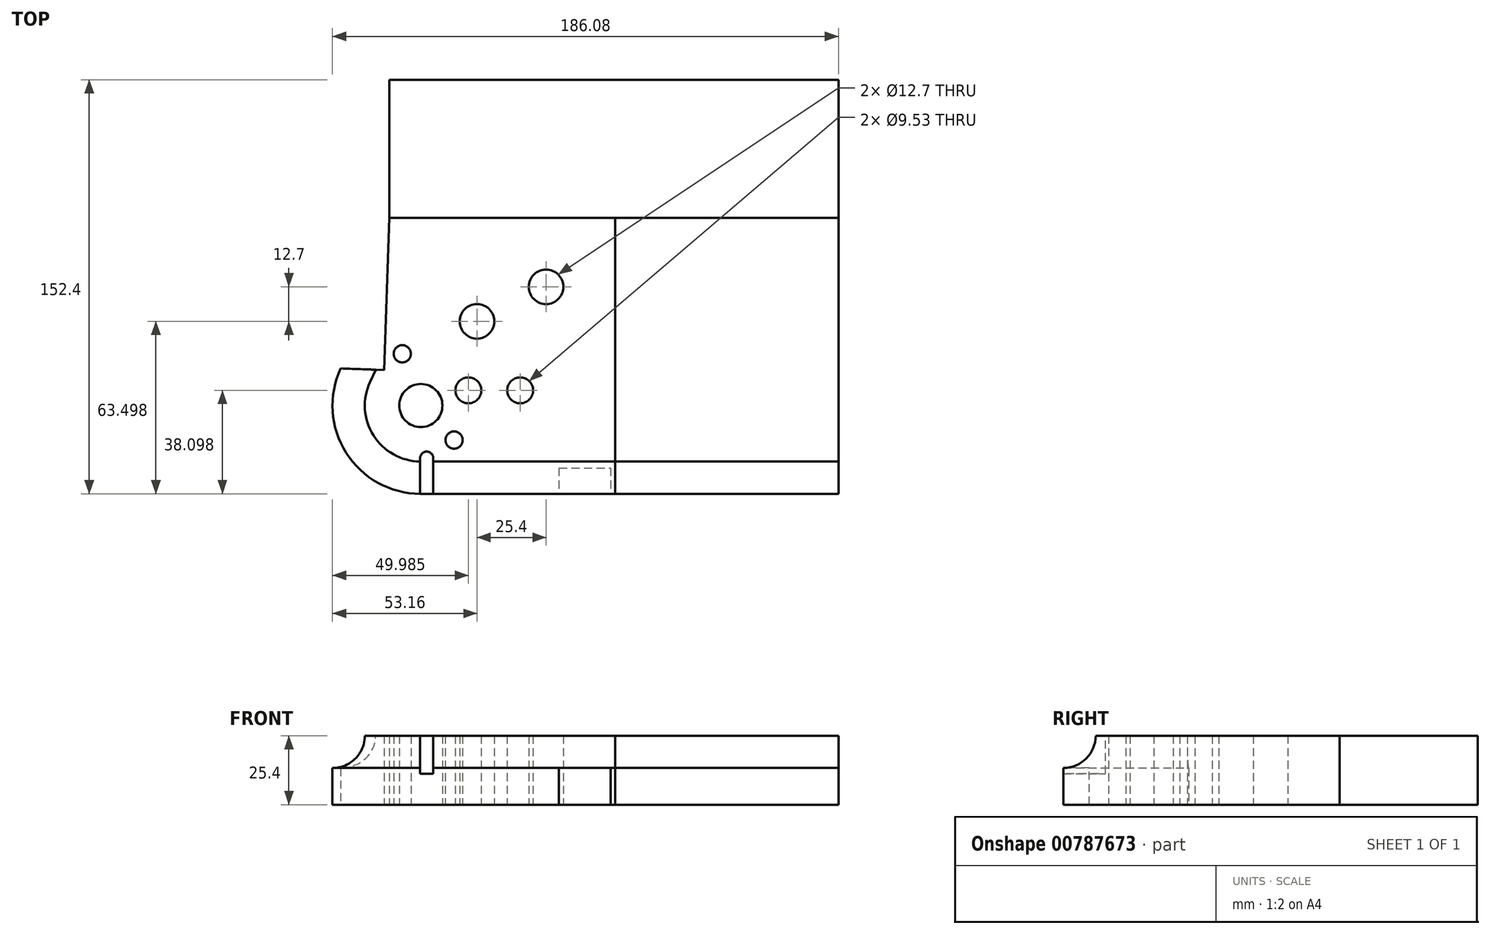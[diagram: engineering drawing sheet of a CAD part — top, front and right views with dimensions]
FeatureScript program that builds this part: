
annotation { "Feature Type Name" : "Feature", "Feature Type Description" : "" }
export const myFeature = defineFeature(function(context is Context, id is Id, definition is map)
    precondition{}
    {
        {
            var Q0;
            Q0=qCreatedBy(makeId("Top.planeOp"),FACE);
            var sketch = newSketch(context, id + "F0", { "sketchPlane" : qUnion([Q0])});
            skArc(sketch, "E0", {"start": v(-29.51, 13.64) * mm, "mid": v(-27.4, -17.51) * mm, "end": v(0, -32.51) * mm});
            skLineSegment(sketch, "E1", {"start": v(0, -32.51) * mm, "end": v(71.45, -32.51) * mm});
            skLineSegment(sketch, "E2", {"start": v(71.45, -32.51) * mm, "end": v(71.45, 69.09) * mm});
            skLineSegment(sketch, "E3", {"start": v(71.45, 69.09) * mm, "end": v(-11.53, 69.09) * mm});
            skLineSegment(sketch, "E4", {"start": v(-13.49, 13.08) * mm, "end": v(-29.51, 13.64) * mm});
            skLineSegment(sketch, "E5", {"start": v(-11.53, 69.09) * mm, "end": v(-13.49, 13.08) * mm});
            skCircle(sketch, "E6", {"center": v(0, 0) * mm, "radius": 7.94 * mm});
            skCircle(sketch, "E7", {"center": v(46.05, 43.69) * mm, "radius": 6.35 * mm});
            skCircle(sketch, "E8", {"center": v(20.65, 30.99) * mm, "radius": 6.35 * mm});
            skCircle(sketch, "E9", {"center": v(-6.83, 19.05) * mm, "radius": 3.18 * mm});
            skCircle(sketch, "E10", {"center": v(17.48, 5.59) * mm, "radius": 4.76 * mm});
            skCircle(sketch, "E11", {"center": v(36.53, 5.59) * mm, "radius": 4.76 * mm});
            skCircle(sketch, "E12", {"center": v(12.22, -12.7) * mm, "radius": 3.18 * mm});
            skSolve(sketch);
        }
        {
            var Q0;
            Q0=makeQuery(id+"F0.imprint","IMPRINT",FACE,{"disambiguationData":[TD([[makeQuery(id+"F0.imprint","IMPRINT",EDGE,{"derivedFrom":sQuery(id+"F0.wireOp",EDGE,"E0")}),1.0]])]});
            extrude(context, id + "F1", {"entities" : qUnion([Q0]), "endBound" : BoundingType.SYMMETRIC, "depth" : 25.4 * mm, "offsetDistance" : 25.4 * mm});
        }
        {
            var Q0;
            Q0=makeQuery(id+"F1.opExtrude","SWEPT_FACE",FACE,{"disambiguationData":[OSD([sQuery(id+"F0.wireOp",EDGE,"E2")])]});
            var sketch = newSketch(context, id + "F2", { "sketchPlane" : qUnion([Q0])});
            skCircle(sketch, "E13", {"center": v(-32.51, 12.7) * mm, "radius": 11.9 * mm});
            skSolve(sketch);
        }
        {
            var Q0;
            {var subQ0=sQuery(id+"F2.wireOp",EDGE,"E13");var subQ1=sQuery(id+"F0.wireOp",EDGE,"E2");var subQ4=makeQuery(id+"F1.opExtrude","CAP_EDGE",EDGE,{"disambiguationData":[OSD([subQ1])],"isStart":false});var subQ5=makeQuery(id+"F2.imprint","INTERSECT",VERTEX,{"derivedFrom":[subQ4,subQ0]});Q0=makeQuery(id+"F2.imprint","IMPRINT",FACE,{"disambiguationData":[TD([[makeQuery(id+"F2.imprint","IMPRINT",EDGE,{"disambiguationData":[TD([[subQ5,1.0]])],"derivedFrom":subQ0}),1.0]])]});}
            var Q1;
            Q1=makeQuery(id+"F1.opExtrude","CAP_EDGE",EDGE,{"disambiguationData":[OSD([sQuery(id+"F0.wireOp",EDGE,"E1")])],"isStart":false});
            var Q2;
            Q2=makeQuery(id+"F1.opExtrude","CAP_EDGE",EDGE,{"disambiguationData":[OSD([sQuery(id+"F0.wireOp",EDGE,"E0")])],"isStart":false});
            sweep(context, id + "F3", {"operationType" : NewBodyOperationType.REMOVE, "profiles" : qUnion([Q0]), "path" : qUnion([Q1, Q2])});
        }
        {
            var Q0;
            Q0=makeQuery(id+"F3.boolean.opBoolean","COPY",FACE,{"derivedFrom":makeQuery(id+"F3.opSweep","CAP_FACE",FACE,{"disambiguationData":[OSD([sQuery(id+"F0.wireOp",EDGE,"E0"),sQuery(id+"F0.wireOp",EDGE,"E1"),sQuery(id+"F0.wireOp",EDGE,"E2"),sQuery(id+"F0.wireOp",EDGE,"E4"),sQuery(id+"F2.wireOp",EDGE,"E13")])],"isStart":false})});
            var Q1;
            Q1=makeQuery(id+"F1.opExtrude","SWEPT_FACE",FACE,{"disambiguationData":[OSD([sQuery(id+"F0.wireOp",EDGE,"E4")])]});
            extrude(context, id + "F4", {"entities" : qUnion([Q0]), "operationType" : NewBodyOperationType.REMOVE, "endBound" : BoundingType.UP_TO_SURFACE, "oppositeDirection" : true, "depth" : 25.4 * mm, "endBoundEntityFace" : qUnion([Q1]), "offsetDistance" : 25.4 * mm});
        }
        {
            var Q0;
            Q0=makeQuery(id+"F1.opExtrude","CAP_FACE",FACE,{"disambiguationData":[OSD([sQuery(id+"F0.wireOp",EDGE,"E0"),sQuery(id+"F0.wireOp",EDGE,"E1"),sQuery(id+"F0.wireOp",EDGE,"E2"),sQuery(id+"F0.wireOp",EDGE,"E3"),sQuery(id+"F0.wireOp",EDGE,"E4"),sQuery(id+"F0.wireOp",EDGE,"E5"),sQuery(id+"F0.wireOp",EDGE,"E6"),sQuery(id+"F0.wireOp",EDGE,"E7"),sQuery(id+"F0.wireOp",EDGE,"E8"),sQuery(id+"F0.wireOp",EDGE,"E9"),sQuery(id+"F0.wireOp",EDGE,"E10"),sQuery(id+"F0.wireOp",EDGE,"E11"),sQuery(id+"F0.wireOp",EDGE,"E12")])],"isStart":false});
            var sketch = newSketch(context, id + "F5", { "sketchPlane" : qUnion([Q0])});
            skCircle(sketch, "E14", {"center": v(2.13, -19.33) * mm, "radius": 2.39 * mm});
            skLineSegment(sketch, "E15", {"start": v(4.52, -19.33) * mm, "end": v(4.52, -32.51) * mm});
            skLineSegment(sketch, "E16", {"start": v(4.52, -32.51) * mm, "end": v(-0.25, -32.51) * mm});
            skLineSegment(sketch, "E17", {"start": v(-0.25, -32.51) * mm, "end": v(-0.25, -19.33) * mm});
            skSolve(sketch);
        }
        {
            var Q0;
            {var subQ0=sQuery(id+"F5.wireOp",EDGE,"E14");var subQ7=makeQuery(id+"F5.imprint","INTERSECT",VERTEX,{"derivedFrom":[subQ0,sQuery(id+"F5.wireOp",EDGE,"E15")]});Q0=makeQuery(id+"F5.imprint","IMPRINT",FACE,{"disambiguationData":[TD([[makeQuery(id+"F5.imprint","IMPRINT",EDGE,{"disambiguationData":[TD([[subQ7,-1.0]])],"derivedFrom":subQ0}),1.0]])]});}
            var Q1;
            {var subQ1=sQuery(id+"F5.wireOp",EDGE,"E16");Q1=makeQuery(id+"F5.imprint","IMPRINT",FACE,{"disambiguationData":[TD([[makeQuery(id+"F5.imprint","IMPRINT",EDGE,{"derivedFrom":subQ1}),-1.0]])]});}
            var Q2;
            {var subQ0=sQuery(id+"F5.wireOp",EDGE,"E14");var subQ1=sQuery(id+"F2.wireOp",EDGE,"E13");var subQ2=sQuery(id+"F0.wireOp",EDGE,"E2");var subQ3=sQuery(id+"F0.wireOp",EDGE,"E1");var subQ4=makeQuery(id+"F3.boolean.opBoolean","COPY",EDGE,{"derivedFrom":makeQuery(id+"F3.opSweep","SWEPT_EDGE",EDGE,{"disambiguationData":[OSD([subQ3,subQ2,subQ1]),TDD([makeQuery(id+"F1.opExtrude","CAP_EDGE",EDGE,{"disambiguationData":[OSD([subQ3])],"isStart":false}),makeQuery(id+"F2.imprint","INTERSECT",VERTEX,{"derivedFrom":[makeQuery(id+"F1.opExtrude","CAP_EDGE",EDGE,{"disambiguationData":[OSD([subQ2])],"isStart":false}),subQ1]})])]})});var subQ5=makeQuery(id+"F5.imprint","INTERSECT",VERTEX,{"disambiguationData":[OD(0.0)],"derivedFrom":[subQ4,subQ0]});Q2=makeQuery(id+"F5.imprint","IMPRINT",FACE,{"disambiguationData":[TD([[makeQuery(id+"F5.imprint","IMPRINT",EDGE,{"disambiguationData":[TD([[subQ5,-1.0]])],"derivedFrom":subQ0}),1.0]])]});}
            var Q3;
            {var subQ0=sQuery(id+"F5.wireOp",EDGE,"E17");var subQ1=sQuery(id+"F5.wireOp",EDGE,"E14");var subQ2=makeQuery(id+"F5.imprint","INTERSECT",VERTEX,{"derivedFrom":[subQ1,subQ0]});Q3=makeQuery(id+"F5.imprint","IMPRINT",FACE,{"disambiguationData":[TD([[makeQuery(id+"F5.imprint","IMPRINT",EDGE,{"disambiguationData":[TD([[subQ2,1.0]])],"derivedFrom":subQ0}),-1.0]])]});}
            var Q4;
            {var subQ0=sQuery(id+"F5.wireOp",EDGE,"E15");var subQ1=sQuery(id+"F5.wireOp",EDGE,"E14");var subQ2=makeQuery(id+"F5.imprint","INTERSECT",VERTEX,{"derivedFrom":[subQ1,subQ0]});Q4=makeQuery(id+"F5.imprint","IMPRINT",FACE,{"disambiguationData":[TD([[makeQuery(id+"F5.imprint","IMPRINT",EDGE,{"disambiguationData":[TD([[subQ2,1.0]])],"derivedFrom":subQ1}),-1.0]])]});}
            extrude(context, id + "F6", {"entities" : qUnion([Q0, Q1, Q2, Q3, Q4]), "operationType" : NewBodyOperationType.REMOVE, "oppositeDirection" : true, "depth" : 13.97 * mm, "offsetDistance" : 25.4 * mm});
        }
        {
            var Q0;
            Q0=makeQuery(id+"F1.opExtrude","SWEPT_FACE",FACE,{"disambiguationData":[OSD([sQuery(id+"F0.wireOp",EDGE,"E2")])]});
            extrude(context, id + "F7", {"entities" : qUnion([Q0]), "depth" : 82.12 * mm, "offsetDistance" : 25.4 * mm});
        }
        {
            var Q0;
            Q0=makeQuery(id+"F7.opExtrude","SWEPT_FACE",FACE,{"disambiguationData":[OSD([sQuery(id+"F0.wireOp",EDGE,"E1"),sQuery(id+"F0.wireOp",EDGE,"E2")])]});
            var sketch = newSketch(context, id + "F8", { "sketchPlane" : qUnion([Q0])});
            skLineSegment(sketch, "E18.bottom", {"start": v(50.8, -12.7) * mm, "end": v(69.85, -12.7) * mm});
            skLineSegment(sketch, "E18.top", {"start": v(50.8, 0.8) * mm, "end": v(69.85, 0.8) * mm});
            skLineSegment(sketch, "E18.left", {"start": v(50.8, -12.7) * mm, "end": v(50.8, 0.8) * mm});
            skLineSegment(sketch, "E18.right", {"start": v(69.85, -12.7) * mm, "end": v(69.85, 0.8) * mm});
            skSolve(sketch);
        }
        {
            var Q0;
            Q0=makeQuery(id+"F8.imprint","IMPRINT",FACE,{"disambiguationData":[TD([[makeQuery(id+"F8.imprint","IMPRINT",EDGE,{"derivedFrom":sQuery(id+"F8.wireOp",EDGE,"E18.bottom")}),1.0]])]});
            extrude(context, id + "F9", {"entities" : qUnion([Q0]), "operationType" : NewBodyOperationType.REMOVE, "oppositeDirection" : true, "depth" : 9.52 * mm, "offsetDistance" : 25.4 * mm});
        }
        {
            var Q0;
            Q0=makeQuery(id+"F7.opExtrude","SWEPT_FACE",FACE,{"disambiguationData":[OSD([sQuery(id+"F0.wireOp",EDGE,"E2"),sQuery(id+"F0.wireOp",EDGE,"E3")])]});
            var sketch = newSketch(context, id + "F10", { "sketchPlane" : qUnion([Q0])});
            skLineSegment(sketch, "E19.bottom", {"start": v(-153.57, 12.7) * mm, "end": v(11.53, 12.7) * mm});
            skLineSegment(sketch, "E19.top", {"start": v(-153.57, -12.7) * mm, "end": v(11.53, -12.7) * mm});
            skLineSegment(sketch, "E19.left", {"start": v(-153.57, 12.7) * mm, "end": v(-153.57, -12.7) * mm});
            skLineSegment(sketch, "E19.right", {"start": v(11.53, 12.7) * mm, "end": v(11.53, -12.7) * mm});
            skSolve(sketch);
        }
        {
            var Q0;
            {var subQ2=sQuery(id+"F10.wireOp",EDGE,"E19.left");Q0=makeQuery(id+"F10.imprint","IMPRINT",FACE,{"disambiguationData":[TD([[makeQuery(id+"F10.imprint","IMPRINT",EDGE,{"derivedFrom":subQ2}),1.0]])]});}
            var Q1;
            {var subQ2=sQuery(id+"F10.wireOp",EDGE,"E19.right");Q1=makeQuery(id+"F10.imprint","IMPRINT",FACE,{"disambiguationData":[TD([[makeQuery(id+"F10.imprint","IMPRINT",EDGE,{"derivedFrom":subQ2}),-1.0]])]});}
            extrude(context, id + "F11", {"entities" : qUnion([Q0, Q1]), "depth" : 50.8 * mm, "offsetDistance" : 25.4 * mm});
        }
    });
